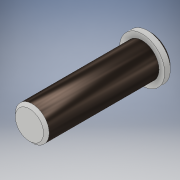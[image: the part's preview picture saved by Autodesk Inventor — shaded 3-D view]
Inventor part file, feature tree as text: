
AUTODESK INVENTOR PART (.ipt)
format: ipt  version: 2017 (Build 210142000, 142)  size: 118,784 bytes
history: native  units: mm
features: extrude x2, chamfer x2, sketch x2
ambient origin geometry x8: Origin, YZ Plane, XZ Plane, XY Plane, X Axis, Y Axis, Z Axis, Center Point
bodies: Solid1 (feature_tree)
feature tree (6):
  extrude  "Extrusion1"  Depth=1.5mm TaperAngle=0.0deg
  extrude  "Extrusion2"  Depth=20.0mm TaperAngle=0.0deg
  chamfer  "Chamfer1"  Distance=0.5mm Angle=45.0deg
  chamfer  "Chamfer2"  Distance=0.5mm Angle=45.0deg
  sketch  "Sketch1"  dims[d0=8.0mm d1=1.5mm d2=0.0mm]
  sketch  "Sketch2"  dims[d4=6.0mm d5=20.0mm d6=0.0mm d7=0.5mm d8=2.0mm d9=45.0deg d10=0.5mm d11=2.0mm d12=45.0deg]
